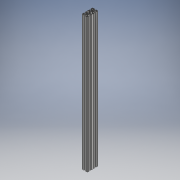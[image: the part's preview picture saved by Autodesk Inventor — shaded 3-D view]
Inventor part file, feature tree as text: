
AUTODESK INVENTOR PART (.ipt)
format: ipt  version: 2018 (Build 220112000, 112)  size: 644,608 bytes
history: native  units: mm
features: other x1, extrude x1, sketch x1
ambient origin geometry x8: Origin, YZ Plane, XZ Plane, XY Plane, X Axis, Y Axis, Z Axis, Center Point
bodies: Body1 (feature_tree)
feature tree (3):
  other  "Sólido1"
  extrude  "Extrusão1"  [1 undecoded]
  sketch  "Esboço1"  dims[d0=1000.0mm d1=0.0mm]
note: 1 required parameter value undecoded (feature->parameter linkage not recoverable at this tier; creation-order binding heuristic only, values carry confidence <= 0.55)
